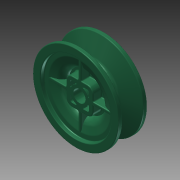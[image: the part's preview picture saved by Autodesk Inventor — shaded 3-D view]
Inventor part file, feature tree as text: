
AUTODESK INVENTOR PART (.ipt)
format: ipt  version: 2015 SP1 (Build 190203100, 203)  size: 1,292,800 bytes
history: native  units: in
note: dims shown in document units (in); Inventor stores cm internally (conversion verified against a paired STEP export)
features: fillet x1, other x1, imported_body x1
ambient origin geometry x8: Origin, YZ Plane, XZ Plane, XY Plane, X Axis, Y Axis, Z Axis, Center Point
bodies: Body1 (feature_tree)
feature tree (3):
  fillet  "Fillet6"  [1 undecoded]
  other  "276-1546-005 Rev31"
  imported_body  "Base1"
note: 1 required parameter value undecoded (feature->parameter linkage not recoverable at this tier; creation-order binding heuristic only, values carry confidence <= 0.55)
